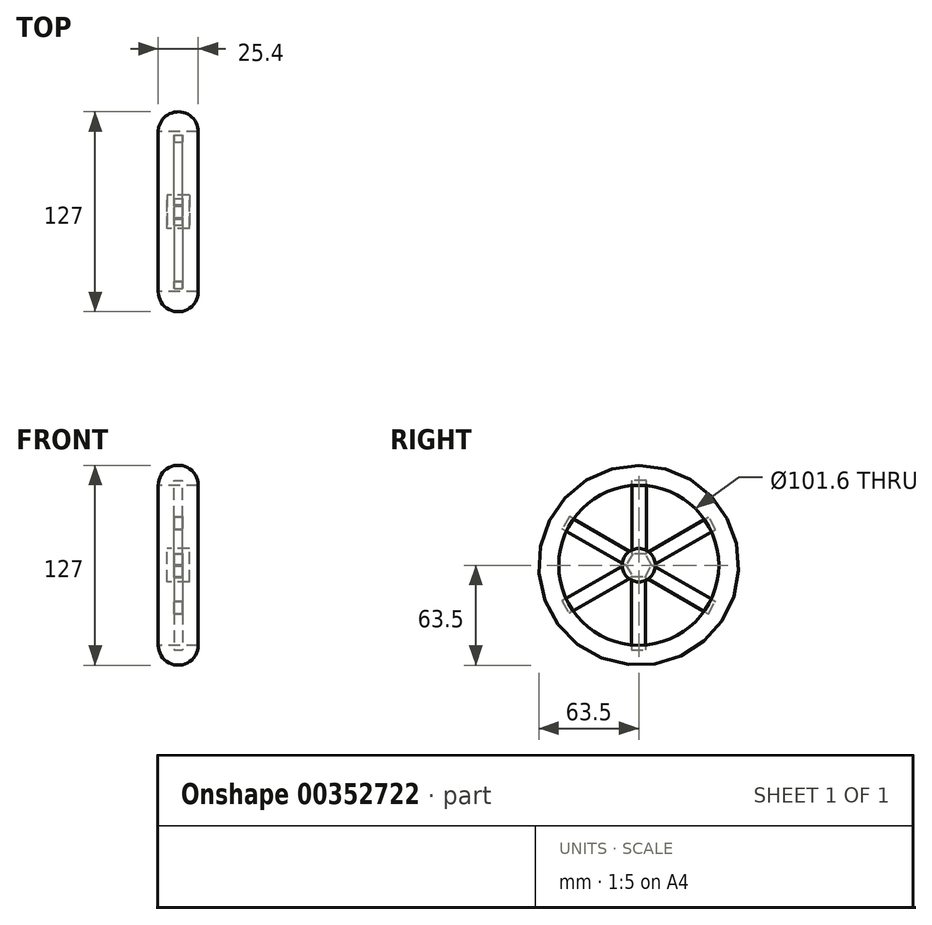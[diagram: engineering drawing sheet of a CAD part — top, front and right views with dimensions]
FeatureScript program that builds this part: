
annotation { "Feature Type Name" : "Feature", "Feature Type Description" : "" }
export const myFeature = defineFeature(function(context is Context, id is Id, definition is map)
    precondition{}
    {
        {
            var Q0;
            Q0=qCreatedBy(makeId("Front.planeOp"),FACE);
            var sketch = newSketch(context, id + "F0", { "sketchPlane" : qUnion([Q0])});
            skLineSegment(sketch, "E0.bottom", {"start": v(12.7, 0) * mm, "end": v(-12.7, 0) * mm});
            skLineSegment(sketch, "E0.top", {"start": v(12.7, 50.8) * mm, "end": v(-12.7, 50.8) * mm});
            skLineSegment(sketch, "E0.left", {"start": v(12.7, 0) * mm, "end": v(12.7, 50.8) * mm});
            skLineSegment(sketch, "E0.right", {"start": v(-12.7, 0) * mm, "end": v(-12.7, 50.8) * mm});
            skPoint(sketch, "E0.middle", {"position": v(0, 25.4) * mm});
            skArc(sketch, "E1", {"start": v(12.7, 50.8) * mm, "mid": v(0, 63.5) * mm, "end": v(-12.7, 50.8) * mm});
            skLineSegment(sketch, "E2", {"start": v(-37.89, 0) * mm, "end": v(38.95, 0) * mm, "construction": true});
            skLineSegment(sketch, "E3", {"start": v(0, 63.5) * mm, "end": v(0, 0) * mm, "construction": true});
            skSolve(sketch);
        }
        {
            var Q0;
            {var subQ0=sQuery(id+"F0.wireOp",EDGE,"E1");Q0=makeQuery(id+"F0.imprint","IMPRINT",FACE,{"disambiguationData":[TD([[makeQuery(id+"F0.imprint","IMPRINT",EDGE,{"derivedFrom":subQ0}),1.0]])]});}
            var Q1;
            Q1=sQuery(id+"F0.wireOp",EDGE,"E2");
            revolve(context, id + "F1", {"entities" : qUnion([Q0]), "axis" : qUnion([Q1]), "revolveType" : RevolveType.FULL});
        }
        {
            var Q0;
            Q0=qCreatedBy(makeId("Right.planeOp"),FACE);
            var sketch = newSketch(context, id + "F2", { "sketchPlane" : qUnion([Q0])});
            skCircle(sketch, "E4", {"center": v(0, 0) * mm, "radius": 10.58 * mm});
            skSolve(sketch);
        }
        {
            var Q0;
            Q0=qSketchRegion(id+"F2",true);
            extrude(context, id + "F3", {"entities" : qUnion([Q0]), "endBound" : BoundingType.SYMMETRIC, "depth" : 14.22 * mm});
        }
        {
            var Q0;
            Q0=qCreatedBy(makeId("Right.planeOp"),FACE);
            var sketch = newSketch(context, id + "F4", { "sketchPlane" : qUnion([Q0])});
            skLineSegment(sketch, "E5.bottom", {"start": v(-4.72, -7.08) * mm, "end": v(4.32, -7.08) * mm});
            skLineSegment(sketch, "E5.top", {"start": v(-4.72, -53.67) * mm, "end": v(4.32, -53.67) * mm});
            skLineSegment(sketch, "E5.left", {"start": v(-4.72, -7.08) * mm, "end": v(-4.72, -53.67) * mm});
            skLineSegment(sketch, "E5.right", {"start": v(4.32, -7.08) * mm, "end": v(4.32, -53.67) * mm});
            skLineSegment(sketch, "E6", {"start": v(-32.24, 0) * mm, "end": v(35.78, 0) * mm, "construction": true});
            skLineSegment(sketch, "E7", {"start": v(0, 36.96) * mm, "end": v(-0.2, -29.68) * mm, "construction": true});
            skPoint(sketch, "E7.endSnap0", {"position": v(-0.2, -7.08) * mm});
            skPoint(sketch, "E8.MirrorCS.end.orphan", {"position": v(4.32, 53.67) * mm});
            skPoint(sketch, "E8.MirrorCS.start.orphan", {"position": v(4.32, 7.08) * mm});
            skPoint(sketch, "E9.MirrorCS.end.orphan", {"position": v(-4.72, 53.67) * mm});
            skPoint(sketch, "E9.MirrorCS.start.orphan", {"position": v(-4.72, 7.08) * mm});
            skSolve(sketch);
        }
        {
            var Q0;
            Q0=qSketchRegion(id+"F4",true);
            extrude(context, id + "F5", {"entities" : qUnion([Q0]), "endBound" : BoundingType.SYMMETRIC, "oppositeDirection" : true, "depth" : 5.6 * mm});
        }
        {
            var Q0;
            Q0=makeQuery(id+"F5.opExtrude","SWEPT_BODY",BODY,{"disambiguationData":[OSD([sQuery(id+"F4.wireOp",EDGE,"E5.bottom"),sQuery(id+"F4.wireOp",EDGE,"E5.top"),sQuery(id+"F4.wireOp",EDGE,"E5.left"),sQuery(id+"F4.wireOp",EDGE,"E5.right")])]});
            var Q1;
            Q1=makeQuery(id+"F3.opExtrude","CAP_EDGE",EDGE,{"disambiguationData":[OSD([sQuery(id+"F2.wireOp",EDGE,"E4")])],"isStart":false});
            circularPattern(context, id + "F6", {"entities" : qUnion([Q0]), "axis" : qUnion([Q1]), "angle" : 360 * degree, "instanceCount" : 6, "equalSpace" : true});
        }
    });
